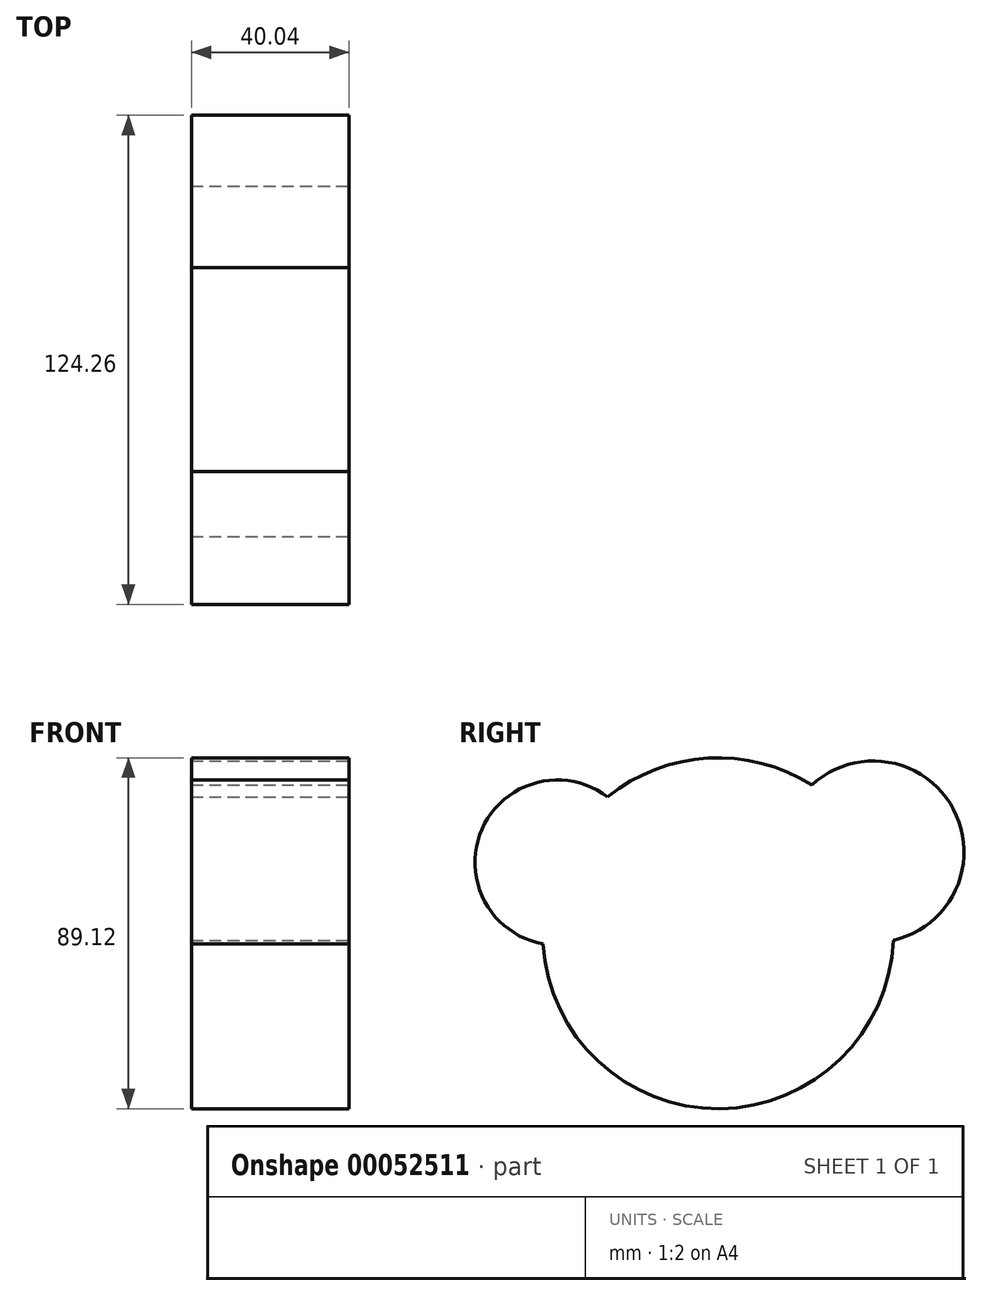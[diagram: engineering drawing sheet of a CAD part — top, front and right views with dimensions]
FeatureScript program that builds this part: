
annotation { "Feature Type Name" : "Feature", "Feature Type Description" : "" }
export const myFeature = defineFeature(function(context is Context, id is Id, definition is map)
    precondition{}
    {
        {
            var Q0;
            Q0=qCreatedBy(makeId("Right.planeOp"),FACE);
            var sketch = newSketch(context, id + "F0", { "sketchPlane" : qUnion([Q0])});
            skCircle(sketch, "E0", {"center": v(0, 0) * mm, "radius": 44.56 * mm});
            skCircle(sketch, "E1", {"center": v(39.45, 20.72) * mm, "radius": 23.06 * mm});
            skCircle(sketch, "E2", {"center": v(-40.77, 17.98) * mm, "radius": 20.98 * mm});
            skLineSegment(sketch, "E3", {"start": v(-40.77, 17.98) * mm, "end": v(39.9, 19.83) * mm});
            skLineSegment(sketch, "E4", {"start": v(0, 18.91) * mm, "end": v(0, -44.56) * mm});
            skLineSegment(sketch, "E5", {"start": v(0, -44.56) * mm, "end": v(0, -56.2) * mm});
            skSolve(sketch);
        }
        {
            var Q0;
            Q0 = qSketchRegion(id + "F0", true);
            extrude(context, id + "F1", {"entities" : qUnion([Q0]), "oppositeDirection" : true, "depth" : 40.04 * mm});
        }
    });
